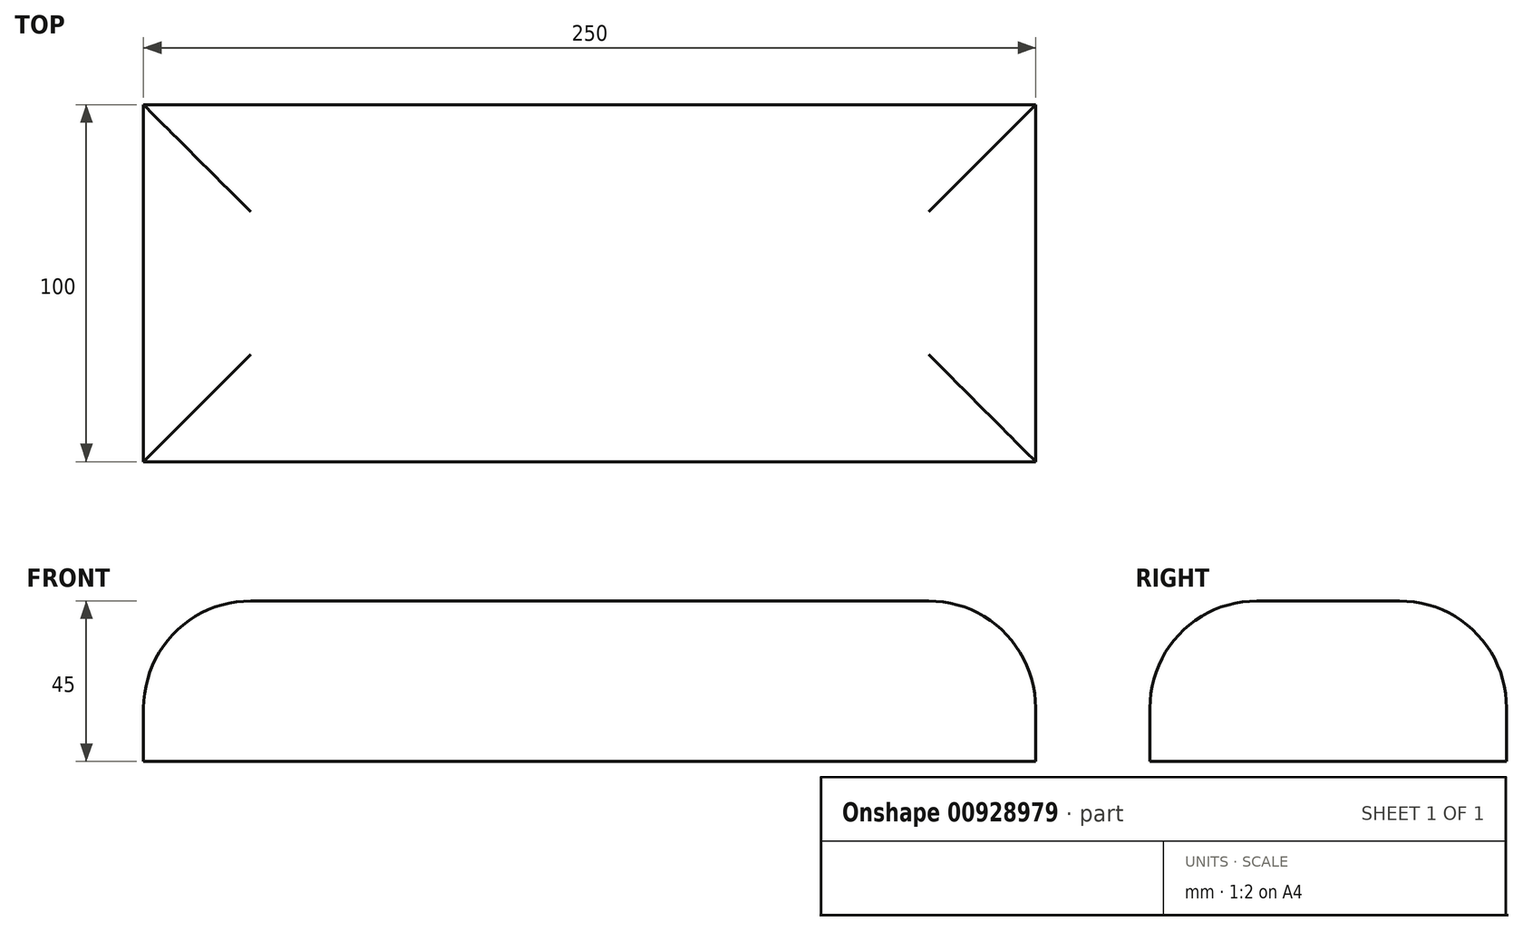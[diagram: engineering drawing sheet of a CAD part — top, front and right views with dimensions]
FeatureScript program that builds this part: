
annotation { "Feature Type Name" : "Feature", "Feature Type Description" : "" }
export const myFeature = defineFeature(function(context is Context, id is Id, definition is map)
    precondition{}
    {
        {
            var Q0;
            Q0=qCreatedBy(makeId("Front.planeOp"),FACE);
            var sketch = newSketch(context, id + "F0", { "sketchPlane" : qUnion([Q0])});
            skLineSegment(sketch, "E0.bottom", {"start": v(-36.35, 45) * mm, "end": v(213.65, 45) * mm});
            skLineSegment(sketch, "E0.top", {"start": v(-36.35, 0) * mm, "end": v(213.65, 0) * mm});
            skLineSegment(sketch, "E0.left", {"start": v(-36.35, 45) * mm, "end": v(-36.35, 0) * mm});
            skLineSegment(sketch, "E0.right", {"start": v(213.65, 45) * mm, "end": v(213.65, 0) * mm});
            skSolve(sketch);
        }
        {
            var Q0;
            Q0=makeQuery(id+"F0.imprint","IMPRINT",FACE,{"disambiguationData":[TD([[makeQuery(id+"F0.imprint","IMPRINT",EDGE,{"derivedFrom":sQuery(id+"F0.wireOp",EDGE,"E0.bottom")}),-1.0]])]});
            extrude(context, id + "F1", {"entities" : qUnion([Q0]), "depth" : 100 * mm, "offsetDistance" : 25 * mm});
        }
        {
            var Q0;
            Q0=makeQuery(id+"F1.opExtrude","CAP_EDGE",EDGE,{"disambiguationData":[OSD([sQuery(id+"F0.wireOp",EDGE,"E0.bottom")])],"isStart":false});
            var Q1;
            Q1=makeQuery(id+"F1.opExtrude","SWEPT_EDGE",EDGE,{"disambiguationData":[OSD([sQuery(id+"F0.wireOp",EDGE,"E0.bottom"),sQuery(id+"F0.wireOp",EDGE,"E0.left")])]});
            var Q2;
            Q2=makeQuery(id+"F1.opExtrude","CAP_EDGE",EDGE,{"disambiguationData":[OSD([sQuery(id+"F0.wireOp",EDGE,"E0.bottom")])],"isStart":true});
            var Q3;
            Q3=makeQuery(id+"F1.opExtrude","SWEPT_EDGE",EDGE,{"disambiguationData":[OSD([sQuery(id+"F0.wireOp",EDGE,"E0.bottom"),sQuery(id+"F0.wireOp",EDGE,"E0.right")])]});
            fillet(context, id + "F2", {"entities" : qUnion([Q0, Q1, Q2, Q3]), "radius" : 30 * mm, "tangentPropagation" : true, "allowEdgeOverflow" : false});
        }
    });
